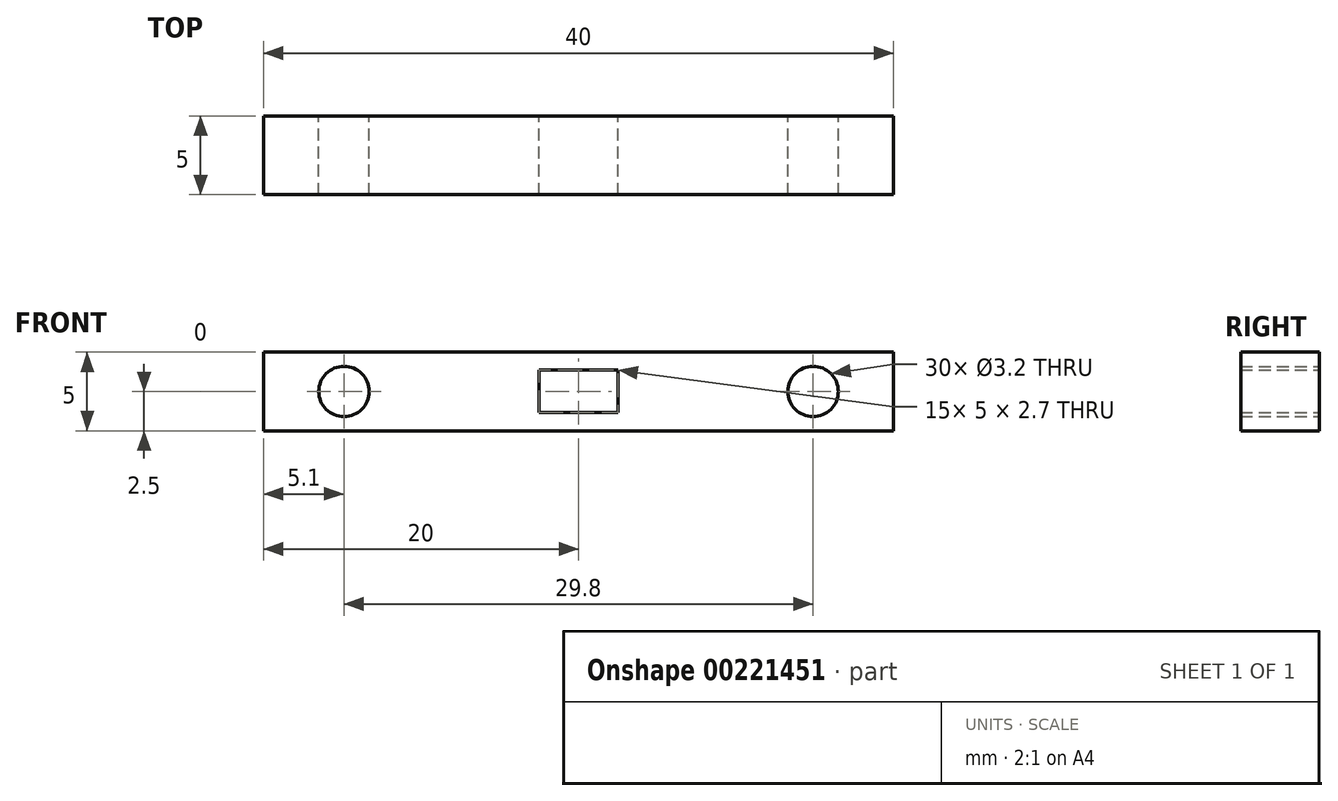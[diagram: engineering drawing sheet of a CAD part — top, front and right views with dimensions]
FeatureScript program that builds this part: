
annotation { "Feature Type Name" : "Feature", "Feature Type Description" : "" }
export const myFeature = defineFeature(function(context is Context, id is Id, definition is map)
    precondition{}
    {
        {
            var Q0;
            Q0=qCreatedBy(makeId("Front.planeOp"),FACE);
            var sketch = newSketch(context, id + "F0", { "sketchPlane" : qUnion([Q0])});
            skLineSegment(sketch, "E0.bottom", {"start": v(20, 2.5) * mm, "end": v(-20, 2.5) * mm});
            skLineSegment(sketch, "E0.top", {"start": v(20, -2.5) * mm, "end": v(-20, -2.5) * mm});
            skLineSegment(sketch, "E0.left", {"start": v(20, 2.5) * mm, "end": v(20, -2.5) * mm});
            skLineSegment(sketch, "E0.right", {"start": v(-20, 2.5) * mm, "end": v(-20, -2.5) * mm});
            skPoint(sketch, "E0.middle", {"position": v(0, 0) * mm});
            skCircle(sketch, "E1", {"center": v(-14.9, 0) * mm, "radius": 1.6 * mm});
            skLineSegment(sketch, "E2", {"start": v(0, 2.5) * mm, "end": v(0, -2.5) * mm, "construction": true});
            skCircle(sketch, "E3.MirrorC", {"center": v(14.9, 0) * mm, "radius": 1.6 * mm});
            skLineSegment(sketch, "E4.bottom", {"start": v(2.5, 1.35) * mm, "end": v(-2.5, 1.35) * mm});
            skLineSegment(sketch, "E4.top", {"start": v(2.5, -1.35) * mm, "end": v(-2.5, -1.35) * mm});
            skLineSegment(sketch, "E4.left", {"start": v(2.5, 1.35) * mm, "end": v(2.5, -1.35) * mm});
            skLineSegment(sketch, "E4.right", {"start": v(-2.5, 1.35) * mm, "end": v(-2.5, -1.35) * mm});
            skSolve(sketch);
        }
        {
            var Q0;
            Q0 = qSketchRegion(id + "F0", true);
            extrude(context, id + "F1", {"entities" : qUnion([Q0]), "depth" : 5 * mm});
        }
    });
